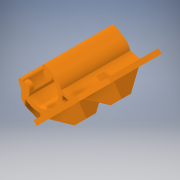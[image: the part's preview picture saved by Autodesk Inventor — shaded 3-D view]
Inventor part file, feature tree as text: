
AUTODESK INVENTOR PART (.ipt)
format: ipt  version: 2017 (Build 210142000, 142)  size: 1,038,848 bytes
history: native  units: in
note: dims shown in document units (in); Inventor stores cm internally (conversion verified against a paired STEP export)
features: other x2, extrude x2, sketch x2
ambient origin geometry x8: Origin, YZ Plane, XZ Plane, XY Plane, X Axis, Y Axis, Z Axis, Center Point
bodies: Solid1 (feature_tree)
feature tree (6):
  other  "10_Support plateau.STEP"
  extrude  "Extrusion1"  TaperAngle=0.0deg  [1 undecoded]
  extrude  "Extrusion3"  [1 undecoded]
  sketch  "Sketch1"  dims[d0=0.3937in d1=0.0in d4=0.0in d5=0.0in]
  sketch  "Sketch3"
  parser-record x1  (decoder bookkeeping rows leaked as tree rows — omitted from the tree; the rows remain in map.json)
note: 2 required parameter values undecoded (feature->parameter linkage not recoverable at this tier; creation-order binding heuristic only, values carry confidence <= 0.55)
